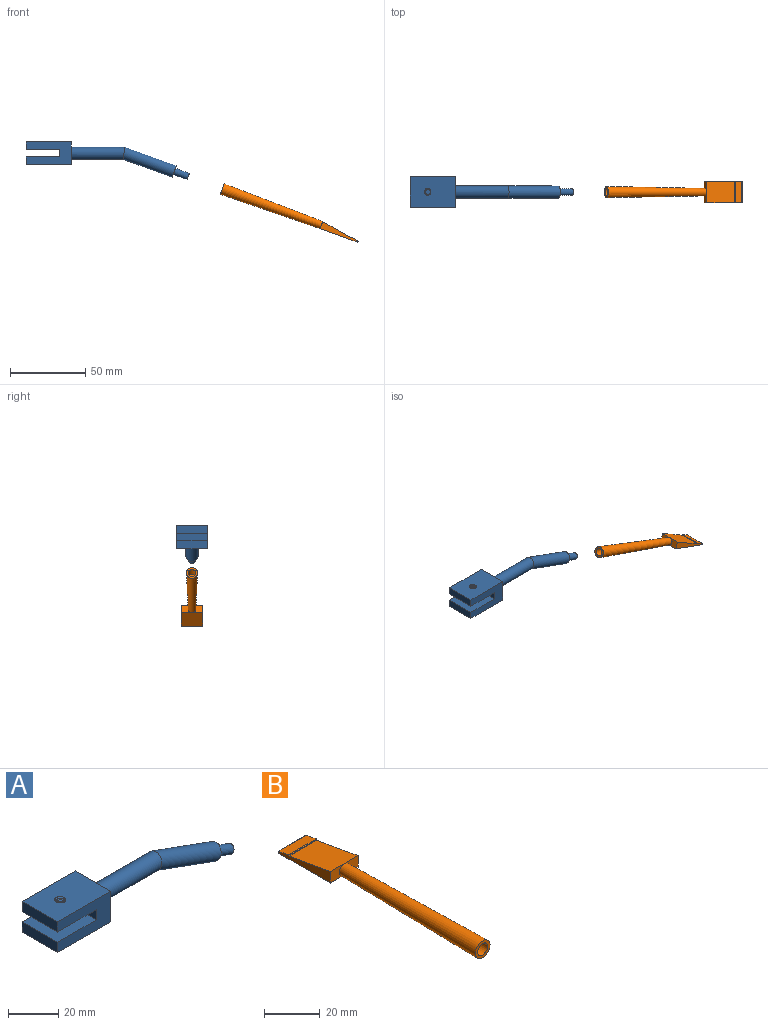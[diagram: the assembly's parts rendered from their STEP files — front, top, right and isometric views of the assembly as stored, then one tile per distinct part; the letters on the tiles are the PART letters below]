
ASSEMBLY  parts=2 mates=1
PART A: 18 faces, bbox 108.9x20.6x26.2 mm
  f0: plane 8x7.52mm, normal (0.94,0,-0.34), area 32.9mm2, adj f1,f3
  f1: cylinder r=4mm len=36.79mm, axis (0.94,0,-0.34), area 892.9mm2, adj f0,f2
  f2: cylinder r=4mm len=35.68mm, axis (1,0,0), area 879mm2, adj f1,f5
  f3: cone r=2.35mm half-angle=1deg, axis (-0.94,0,0.34), area 139.5mm2, adj f0,f4
  f4: plane 4.36x4.1mm, normal (0.94,0,-0.34), area 14.9mm2, adj f3
  f5: plane 20x15mm, normal (1,0,0), area 249.7mm2, adj f2,f6,f12,f13,f14
  f6: plane 30.54x20.54mm, normal (0,0,1), area 585.1mm2, adj f5,f7,f13,f14,f15,f16,f17
  f7: plane 20x5mm, normal (-1,0,0), area 100mm2, adj f6,f8,f13,f14
  f8: plane 22.58x20.58mm, normal (0,0,-1), area 425.1mm2, adj f7,f9,f13,f14,f15,f16,f17
  f9: plane 20x5mm, normal (-1,0,0), area 100mm2, adj f8,f10,f13,f14
  f10: plane 22x20mm, normal (0,0,1), area 440mm2, adj f9,f11,f13,f14
  f11: plane 20x5mm, normal (-1,0,0), area 100mm2, adj f10,f12,f13,f14
  f12: plane 30x20mm, normal (0,0,-1), area 600mm2, adj f5,f11,f13,f14
  f13: plane 30x15mm, normal (0,-1,0), area 340mm2, adj f5,f6,f7,f8,f9,f10,f11,f12
  f14: plane 30x15mm, normal (0,1,0), area 340mm2, adj f5,f6,f7,f8,f9,f10,f11,f12
  f15: cylinder r=1.82mm len=5mm, axis (0,0,1), area 0.6mm2, adj f6,f8,f16,f17
  f16: bspline ~5.82x5.79mm, area 67.7mm2, adj f6,f8,f15,f17
  f17: bspline ~5.95x5.79mm, area 67.7mm2, adj f6,f8,f15,f16
PART B: 14 faces, bbox 14x96.5x7.4 mm
  f0: cone r=2.5mm half-angle=1deg, axis (0,-1,0), area 1368.5mm2, adj f1,f2,f8
  f1: plane 7.44x7.44mm, normal (0,-1,0), area 23.9mm2, adj f0,f12
  f2: plane 7x5mm, normal (0,-1,0), area 25.2mm2, adj f0,f7,f9,f10
  f3: cylinder r=0.46mm len=14mm, axis (-1,0,0), area 19mm2, adj f4,f9,f10,f11
  f4: plane 14x4.92mm, normal (0,0.17,0.98), area 70mm2, adj f3,f5,f10,f11
  f5: cylinder r=0.2mm len=14mm, axis (-1,0,0), area 4.4mm2, adj f4,f6,f10,f11
  f6: plane 14x0.3mm, normal (0,-0.98,0.17), area 4.2mm2, adj f5,f7,f10,f11
  f7: plane 20.87x14mm, normal (0,0.17,0.98), area 296.7mm2, adj f2,f6,f8,f10,f11
  f8: plane 7x5mm, normal (0,-1,0), area 25.2mm2, adj f0,f7,f9,f11
  f9: plane 26x14mm, normal (0,0,-1), area 364mm2, adj f2,f3,f8,f10,f11
  f10: plane 26.46x5mm, normal (1,0,0), area 73.3mm2, adj f2,f3,f4,f5,f6,f7,f9
  f11: plane 26.46x5mm, normal (-1,0,0), area 73.3mm2, adj f3,f4,f5,f6,f7,f8,f9
  f12: cone r=2.5mm half-angle=1deg, axis (0,1,0), area 162.6mm2, adj f1,f13
  f13: plane 5.35x5.35mm, normal (0,-1,0), area 22.5mm2, adj f12
PLACE A t=(-62.59,0,-24.16)mm
PLACE B rot(axis=(-0.17,0.17,-0.97),91.7deg) t=(103.44,0,-71.86)mm
MATE slider B.f0 <-> A.f1  axis (-0.94,0,0.34) through (37.67,0,-47.92)mm
